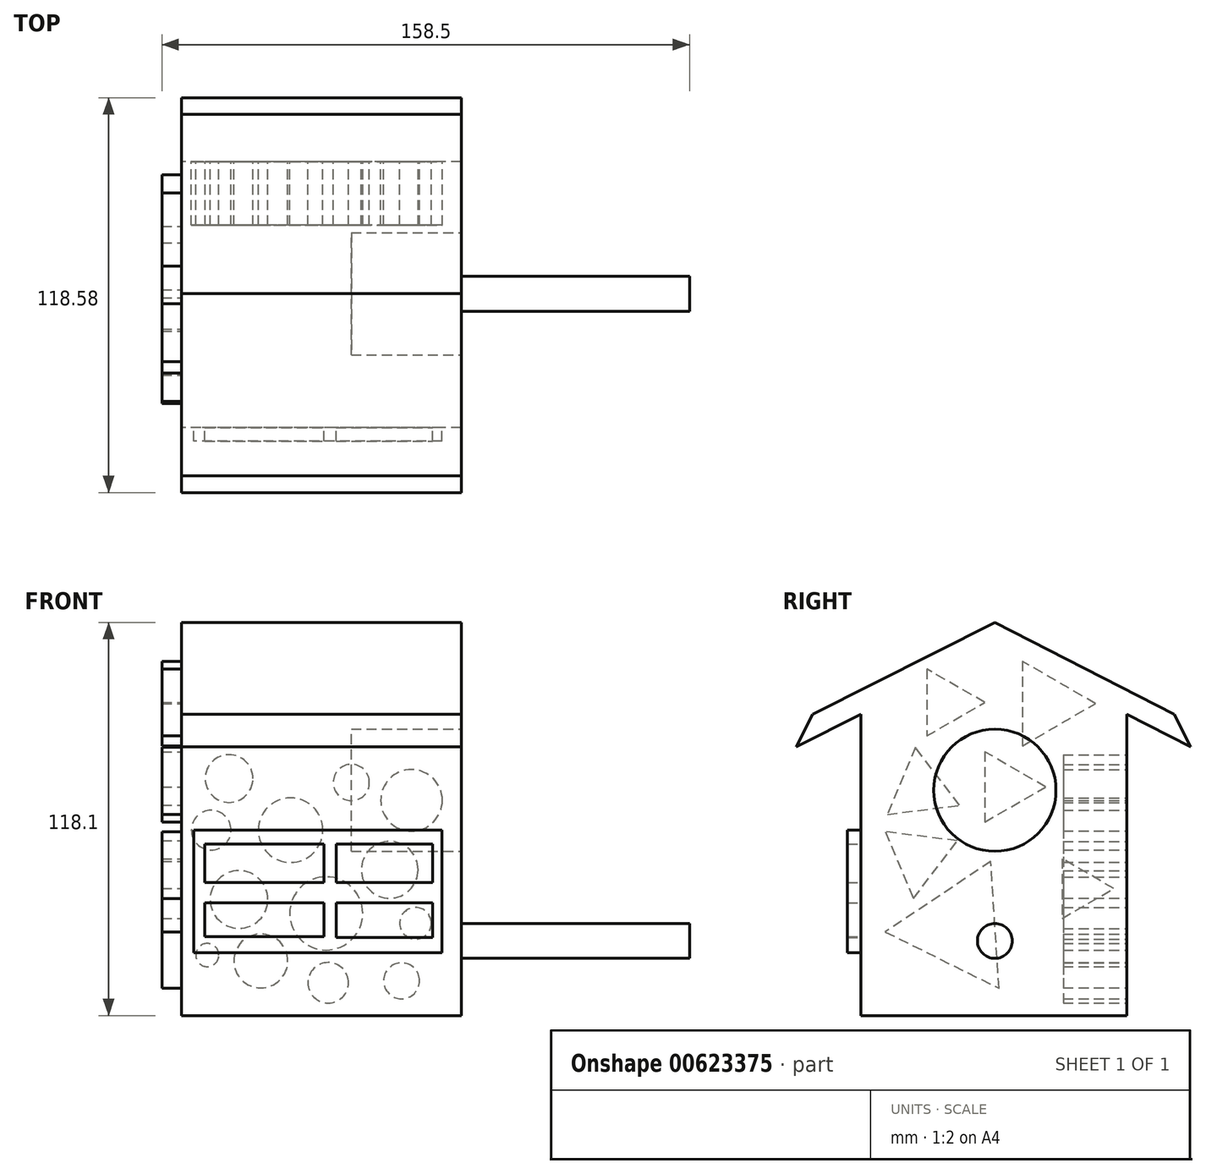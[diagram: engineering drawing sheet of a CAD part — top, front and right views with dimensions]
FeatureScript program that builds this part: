
annotation { "Feature Type Name" : "Feature", "Feature Type Description" : "" }
export const myFeature = defineFeature(function(context is Context, id is Id, definition is map)
    precondition{}
    {
        {
            var Q0;
            Q0=qCreatedBy(makeId("Right.planeOp"),FACE);
            var sketch = newSketch(context, id + "F0", { "sketchPlane" : qUnion([Q0])});
            skLineSegment(sketch, "E0", {"start": v(-40.21, 34.85) * mm, "end": v(-40.21, -55.7) * mm});
            skLineSegment(sketch, "E1", {"start": v(-40.21, -55.7) * mm, "end": v(39.61, -55.7) * mm});
            skLineSegment(sketch, "E2", {"start": v(39.61, -55.7) * mm, "end": v(39.61, 34.85) * mm});
            skLineSegment(sketch, "E3", {"start": v(39.61, 34.85) * mm, "end": v(0, 55.1) * mm});
            skLineSegment(sketch, "E4", {"start": v(0, 55.1) * mm, "end": v(-40.21, 34.85) * mm});
            skLineSegment(sketch, "E5", {"start": v(-40.21, 34.85) * mm, "end": v(-59.73, 25.02) * mm});
            skLineSegment(sketch, "E6", {"start": v(-59.73, 25.02) * mm, "end": v(-54.7, 34.85) * mm});
            skLineSegment(sketch, "E7", {"start": v(-54.7, 34.85) * mm, "end": v(0, 62.4) * mm});
            skLineSegment(sketch, "E8", {"start": v(0, 62.4) * mm, "end": v(53.9, 34.85) * mm});
            skLineSegment(sketch, "E9", {"start": v(53.9, 34.85) * mm, "end": v(58.85, 25.02) * mm});
            skLineSegment(sketch, "E10", {"start": v(58.85, 25.02) * mm, "end": v(39.61, 34.85) * mm});
            skSolve(sketch);
        }
        {
            var Q0;
            Q0 = qSketchRegion(id + "F0", true);
            extrude(context, id + "F1", {"entities" : qUnion([Q0]), "depth" : 33.02 * mm, "offsetDistance" : 25.4 * mm});
        }
        {
            var Q0;
            Q0=makeQuery(id+"F1.opExtrude","CAP_FACE",FACE,{"disambiguationData":[OSD([sQuery(id+"F0.wireOp",EDGE,"E0"),sQuery(id+"F0.wireOp",EDGE,"E1"),sQuery(id+"F0.wireOp",EDGE,"E2"),sQuery(id+"F0.wireOp",EDGE,"E5"),sQuery(id+"F0.wireOp",EDGE,"E6"),sQuery(id+"F0.wireOp",EDGE,"E7"),sQuery(id+"F0.wireOp",EDGE,"E8"),sQuery(id+"F0.wireOp",EDGE,"E9"),sQuery(id+"F0.wireOp",EDGE,"E10")])],"isStart":false});
            var sketch = newSketch(context, id + "F2", { "sketchPlane" : qUnion([Q0])});
            skCircle(sketch, "E11", {"center": v(0, 12) * mm, "radius": 18.36 * mm});
            skSolve(sketch);
        }
        {
            var Q0;
            Q0 = qSketchRegion(id + "F2", true);
            extrude(context, id + "F3", {"entities" : qUnion([Q0]), "operationType" : NewBodyOperationType.REMOVE, "oppositeDirection" : true, "depth" : 38.1 * mm, "offsetDistance" : 25.4 * mm});
        }
        {
            var Q0;
            Q0=makeQuery(id+"F1.opExtrude","CAP_FACE",FACE,{"disambiguationData":[OSD([sQuery(id+"F0.wireOp",EDGE,"E0"),sQuery(id+"F0.wireOp",EDGE,"E1"),sQuery(id+"F0.wireOp",EDGE,"E2"),sQuery(id+"F0.wireOp",EDGE,"E5"),sQuery(id+"F0.wireOp",EDGE,"E6"),sQuery(id+"F0.wireOp",EDGE,"E7"),sQuery(id+"F0.wireOp",EDGE,"E8"),sQuery(id+"F0.wireOp",EDGE,"E9"),sQuery(id+"F0.wireOp",EDGE,"E10")])],"isStart":false});
            var sketch = newSketch(context, id + "F4", { "sketchPlane" : qUnion([Q0])});
            skCircle(sketch, "E12", {"center": v(0, -33.28) * mm, "radius": 5.25 * mm});
            skSolve(sketch);
        }
        {
            var Q0;
            Q0 = qSketchRegion(id + "F4", true);
            extrude(context, id + "F5", {"entities" : qUnion([Q0]), "operationType" : NewBodyOperationType.ADD, "depth" : 68.58 * mm, "offsetDistance" : 25.4 * mm});
        }
        {
            var Q0;
            Q0=makeQuery(id+"F1.opExtrude","CAP_FACE",FACE,{"disambiguationData":[OSD([sQuery(id+"F0.wireOp",EDGE,"E0"),sQuery(id+"F0.wireOp",EDGE,"E1"),sQuery(id+"F0.wireOp",EDGE,"E2"),sQuery(id+"F0.wireOp",EDGE,"E5"),sQuery(id+"F0.wireOp",EDGE,"E6"),sQuery(id+"F0.wireOp",EDGE,"E7"),sQuery(id+"F0.wireOp",EDGE,"E8"),sQuery(id+"F0.wireOp",EDGE,"E9"),sQuery(id+"F0.wireOp",EDGE,"E10")])],"isStart":true});
            var sketch = newSketch(context, id + "F6", { "sketchPlane" : qUnion([Q0])});
            skLineSegment(sketch, "E13", {"start": v(-58.85, 25.02) * mm, "end": v(-53.9, 34.85) * mm});
            skLineSegment(sketch, "E14", {"start": v(-53.9, 34.85) * mm, "end": v(0, 62.4) * mm});
            skLineSegment(sketch, "E15", {"start": v(0, 62.4) * mm, "end": v(54.7, 34.85) * mm});
            skLineSegment(sketch, "E16", {"start": v(54.7, 34.85) * mm, "end": v(59.73, 25.02) * mm});
            skLineSegment(sketch, "E17", {"start": v(59.73, 25.02) * mm, "end": v(40.21, 34.85) * mm});
            skLineSegment(sketch, "E18", {"start": v(40.21, 34.85) * mm, "end": v(40.21, -55.7) * mm});
            skLineSegment(sketch, "E19", {"start": v(40.21, -55.7) * mm, "end": v(-39.61, -55.7) * mm});
            skLineSegment(sketch, "E20", {"start": v(-39.61, -55.7) * mm, "end": v(-39.61, 34.85) * mm});
            skLineSegment(sketch, "E21", {"start": v(-39.61, 34.85) * mm, "end": v(-58.85, 25.02) * mm});
            skSolve(sketch);
        }
        {
            var Q0;
            Q0 = qSketchRegion(id + "F6", true);
            extrude(context, id + "F7", {"entities" : qUnion([Q0]), "operationType" : NewBodyOperationType.ADD, "depth" : 51.05 * mm, "offsetDistance" : 25.4 * mm});
        }
        {
            var Q0;
            Q0=makeQuery(id+"F7.boolean.opBoolean","MERGE",FACE,{"derivedFrom":[makeQuery(id+"F1.opExtrude","SWEPT_FACE",FACE,{"disambiguationData":[OSD([sQuery(id+"F0.wireOp",EDGE,"E2")])]}),makeQuery(id+"F7.opExtrude","SWEPT_FACE",FACE,{"disambiguationData":[OSD([sQuery(id+"F6.wireOp",EDGE,"E20")])]})]});
            var sketch = newSketch(context, id + "F8", { "sketchPlane" : qUnion([Q0])});
            skCircle(sketch, "E22", {"center": v(-19.28, -28) * mm, "radius": 4.77 * mm});
            skCircle(sketch, "E23", {"center": v(7.53, -25.02) * mm, "radius": 10.98 * mm});
            skCircle(sketch, "E24", {"center": v(18.25, 0) * mm, "radius": 9.7 * mm});
            skCircle(sketch, "E25", {"center": v(-18.09, 8.94) * mm, "radius": 9.25 * mm});
            skCircle(sketch, "E26", {"center": v(-11.54, -11.91) * mm, "radius": 8.53 * mm});
            skCircle(sketch, "E27", {"center": v(36.72, 15.49) * mm, "radius": 7.17 * mm});
            skCircle(sketch, "E28", {"center": v(33.74, -20.85) * mm, "radius": 8.67 * mm});
            skCircle(sketch, "E29", {"center": v(0, 14.3) * mm, "radius": 5.45 * mm});
            skCircle(sketch, "E30", {"center": v(27.19, -39.32) * mm, "radius": 8.1 * mm});
            skCircle(sketch, "E31", {"center": v(-15.1, -45.27) * mm, "radius": 5.4 * mm});
            skCircle(sketch, "E32", {"center": v(6.93, -45.87) * mm, "radius": 6.08 * mm});
            skCircle(sketch, "E33", {"center": v(42.08, 0) * mm, "radius": 5.96 * mm});
            skCircle(sketch, "E34", {"center": v(43.27, -37.53) * mm, "radius": 3.47 * mm});
            skSolve(sketch);
        }
        {
            var Q0;
            Q0 = qSketchRegion(id + "F8", true);
            extrude(context, id + "F9", {"entities" : qUnion([Q0]), "operationType" : NewBodyOperationType.REMOVE, "oppositeDirection" : true, "depth" : 19.05 * mm, "offsetDistance" : 25.4 * mm});
        }
        {
            var Q0;
            Q0=makeQuery(id+"F7.boolean.opBoolean","MERGE",FACE,{"derivedFrom":[makeQuery(id+"F1.opExtrude","SWEPT_FACE",FACE,{"disambiguationData":[OSD([sQuery(id+"F0.wireOp",EDGE,"E0")])]}),makeQuery(id+"F7.opExtrude","SWEPT_FACE",FACE,{"disambiguationData":[OSD([sQuery(id+"F6.wireOp",EDGE,"E18")])]})]});
            var sketch = newSketch(context, id + "F10", { "sketchPlane" : qUnion([Q0])});
            skSolve(sketch);
        }
        {
            var Q0;
            {var subQ0=sQuery(id+"F0.wireOp",EDGE,"E0");Q0=makeQuery(id+"F10.imprint","IMPRINT",FACE,{"disambiguationData":[TD([[makeQuery(id+"F10.imprint","IMPRINT",EDGE,{"derivedFrom":makeQuery(id+"F1.opExtrude","CAP_EDGE",EDGE,{"disambiguationData":[OSD([subQ0])],"isStart":false})}),-1.0]])]});}
            var sketch = newSketch(context, id + "F11", { "sketchPlane" : qUnion([Q0])});
            skLineSegment(sketch, "E35", {"start": v(-47.34, 0) * mm, "end": v(-47.34, -36.84) * mm});
            skLineSegment(sketch, "E36", {"start": v(-47.34, -36.84) * mm, "end": v(27.17, -36.84) * mm});
            skLineSegment(sketch, "E37", {"start": v(27.17, -36.84) * mm, "end": v(27.17, 0) * mm});
            skLineSegment(sketch, "E38", {"start": v(27.17, 0) * mm, "end": v(-47.34, 0) * mm});
            skLineSegment(sketch, "E39.bottom", {"start": v(-43.98, -4.16) * mm, "end": v(-8.25, -4.16) * mm});
            skLineSegment(sketch, "E39.top", {"start": v(-43.98, -15.77) * mm, "end": v(-8.25, -15.77) * mm});
            skLineSegment(sketch, "E39.left", {"start": v(-43.98, -4.16) * mm, "end": v(-43.98, -15.77) * mm});
            skLineSegment(sketch, "E39.right", {"start": v(-8.25, -4.16) * mm, "end": v(-8.25, -15.77) * mm});
            skLineSegment(sketch, "E40.bottom", {"start": v(-4.59, -4.16) * mm, "end": v(24.42, -4.16) * mm});
            skLineSegment(sketch, "E40.top", {"start": v(-4.59, -15.77) * mm, "end": v(24.42, -15.77) * mm});
            skLineSegment(sketch, "E40.left", {"start": v(-4.59, -4.16) * mm, "end": v(-4.59, -15.77) * mm});
            skLineSegment(sketch, "E40.right", {"start": v(24.42, -4.16) * mm, "end": v(24.42, -15.77) * mm});
            skLineSegment(sketch, "E41.bottom", {"start": v(-8.25, -21.88) * mm, "end": v(-43.98, -21.88) * mm});
            skLineSegment(sketch, "E41.top", {"start": v(-8.25, -31.95) * mm, "end": v(-43.98, -31.95) * mm});
            skLineSegment(sketch, "E41.left", {"start": v(-8.25, -21.88) * mm, "end": v(-8.25, -31.95) * mm});
            skLineSegment(sketch, "E41.right", {"start": v(-43.98, -21.88) * mm, "end": v(-43.98, -31.95) * mm});
            skPoint(sketch, "E42.firstSnap0", {"position": v(-26.12, -21.88) * mm});
            skLineSegment(sketch, "E42.bottom", {"start": v(-4.59, -21.88) * mm, "end": v(24.42, -21.88) * mm});
            skLineSegment(sketch, "E42.top", {"start": v(-4.59, -32.26) * mm, "end": v(24.42, -32.26) * mm});
            skLineSegment(sketch, "E42.left", {"start": v(-4.59, -21.88) * mm, "end": v(-4.59, -32.26) * mm});
            skLineSegment(sketch, "E42.right", {"start": v(24.42, -21.88) * mm, "end": v(24.42, -32.26) * mm});
            skSolve(sketch);
        }
        {
            var Q0;
            Q0 = qSketchRegion(id + "F11", true);
            extrude(context, id + "F12", {"entities" : qUnion([Q0]), "operationType" : NewBodyOperationType.ADD, "depth" : 4.06 * mm, "offsetDistance" : 25.4 * mm});
        }
        {
            var Q0;
            Q0=makeQuery(id+"F7.opExtrude","CAP_FACE",FACE,{"disambiguationData":[OSD([sQuery(id+"F6.wireOp",EDGE,"E13"),sQuery(id+"F6.wireOp",EDGE,"E14"),sQuery(id+"F6.wireOp",EDGE,"E15"),sQuery(id+"F6.wireOp",EDGE,"E16"),sQuery(id+"F6.wireOp",EDGE,"E17"),sQuery(id+"F6.wireOp",EDGE,"E18"),sQuery(id+"F6.wireOp",EDGE,"E19"),sQuery(id+"F6.wireOp",EDGE,"E20"),sQuery(id+"F6.wireOp",EDGE,"E21")])],"isStart":false});
            var sketch = newSketch(context, id + "F13", { "sketchPlane" : qUnion([Q0])});
            skCircle(sketch, "E43.cCircle", {"center": v(-3.07, 12.97) * mm, "radius": 6.1 * mm, "construction": true});
            skLineSegment(sketch, "E43.0", {"start": v(3.04, 23.55) * mm, "end": v(3.04, 2.4) * mm});
            skLineSegment(sketch, "E43.1", {"start": v(3.04, 2.4) * mm, "end": v(-15.28, 12.97) * mm});
            skLineSegment(sketch, "E43.2", {"start": v(-15.28, 12.97) * mm, "end": v(3.04, 23.55) * mm});
            skPoint(sketch, "E43.0.midPoint", {"position": v(3.04, 12.97) * mm});
            skCircle(sketch, "E44.cCircle", {"center": v(-15.6, 38.01) * mm, "radius": 7.33 * mm, "construction": true});
            skLineSegment(sketch, "E44.0", {"start": v(-8.26, 50.7) * mm, "end": v(-8.26, 25.32) * mm});
            skLineSegment(sketch, "E44.1", {"start": v(-8.26, 25.32) * mm, "end": v(-30.25, 38.01) * mm});
            skLineSegment(sketch, "E44.2", {"start": v(-30.25, 38.01) * mm, "end": v(-8.26, 50.7) * mm});
            skPoint(sketch, "E44.0.midPoint", {"position": v(-8.26, 38.01) * mm});
            skCircle(sketch, "E45.cCircle", {"center": v(10.98, -29.17) * mm, "radius": 11.01 * mm, "construction": true});
            skLineSegment(sketch, "E45.0", {"start": v(1.22, -9.43) * mm, "end": v(32.95, -30.59) * mm});
            skLineSegment(sketch, "E45.1", {"start": v(32.95, -30.59) * mm, "end": v(-1.24, -47.5) * mm});
            skLineSegment(sketch, "E45.2", {"start": v(-1.24, -47.5) * mm, "end": v(1.22, -9.43) * mm});
            skPoint(sketch, "E45.0.midPoint", {"position": v(17.09, -20) * mm});
            skCircle(sketch, "E46.cCircle", {"center": v(22.28, 12.36) * mm, "radius": 6.3 * mm, "construction": true});
            skLineSegment(sketch, "E46.0", {"start": v(23.85, 24.85) * mm, "end": v(32.31, 4.75) * mm});
            skLineSegment(sketch, "E46.1", {"start": v(32.31, 4.75) * mm, "end": v(10.67, 7.47) * mm});
            skLineSegment(sketch, "E46.2", {"start": v(10.67, 7.47) * mm, "end": v(23.85, 24.85) * mm});
            skPoint(sketch, "E46.0.midPoint", {"position": v(28.08, 14.8) * mm});
            skCircle(sketch, "E47.cCircle", {"center": v(-25.36, -17.57) * mm, "radius": 5.2 * mm, "construction": true});
            skLineSegment(sketch, "E47.0", {"start": v(-20.17, -8.57) * mm, "end": v(-20.17, -26.56) * mm});
            skLineSegment(sketch, "E47.1", {"start": v(-20.17, -26.56) * mm, "end": v(-35.75, -17.57) * mm});
            skLineSegment(sketch, "E47.2", {"start": v(-35.75, -17.57) * mm, "end": v(-20.17, -8.57) * mm});
            skPoint(sketch, "E47.0.midPoint", {"position": v(-20.17, -17.57) * mm});
            skCircle(sketch, "E48.cCircle", {"center": v(14.64, 38.32) * mm, "radius": 5.8 * mm, "construction": true});
            skLineSegment(sketch, "E48.0", {"start": v(20.44, 48.37) * mm, "end": v(20.44, 28.27) * mm});
            skLineSegment(sketch, "E48.1", {"start": v(20.44, 28.27) * mm, "end": v(3.04, 38.32) * mm});
            skLineSegment(sketch, "E48.2", {"start": v(3.04, 38.32) * mm, "end": v(20.44, 48.37) * mm});
            skPoint(sketch, "E48.0.midPoint", {"position": v(20.44, 38.32) * mm});
            skCircle(sketch, "E49.cCircle", {"center": v(22.89, -8.1) * mm, "radius": 6.3 * mm, "construction": true});
            skLineSegment(sketch, "E49.0", {"start": v(32.92, -0.5) * mm, "end": v(24.46, -20.6) * mm});
            skLineSegment(sketch, "E49.1", {"start": v(24.46, -20.6) * mm, "end": v(11.28, -3.21) * mm});
            skLineSegment(sketch, "E49.2", {"start": v(11.28, -3.21) * mm, "end": v(32.92, -0.5) * mm});
            skPoint(sketch, "E49.0.midPoint", {"position": v(28.7, -10.54) * mm});
            skSolve(sketch);
        }
        {
            var Q0;
            Q0 = qSketchRegion(id + "F13", true);
            extrude(context, id + "F14", {"entities" : qUnion([Q0]), "operationType" : NewBodyOperationType.ADD, "depth" : 5.84 * mm, "offsetDistance" : 25.4 * mm});
        }
    });
